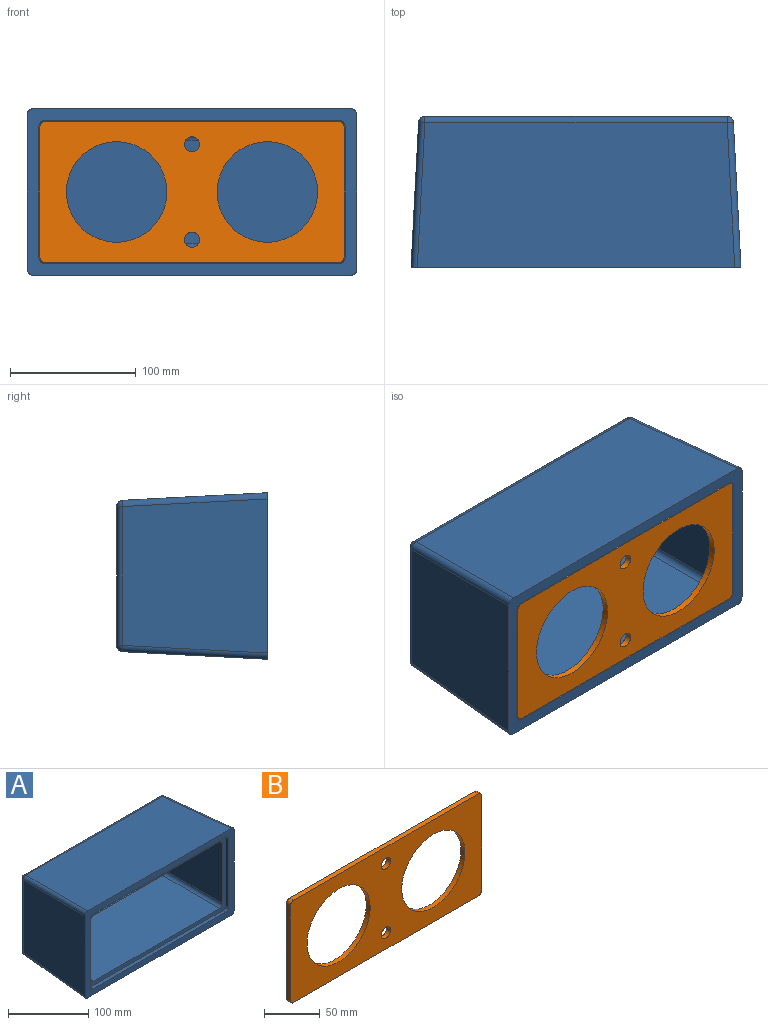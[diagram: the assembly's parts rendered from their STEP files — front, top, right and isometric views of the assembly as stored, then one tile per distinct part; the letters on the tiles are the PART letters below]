
ASSEMBLY  parts=2 mates=1
PART A: 44 faces, bbox 262.6x120.1x132.6 mm
  f0: plane 262.58x132.58mm, normal (0,-1,0), area 6996.1mm2, adj f1,f2,f3,f4,f6,f8,f11,f17
  f1: plane 252.59x115.26mm, normal (0,0.05,1), area 28456.9mm2, adj f0,f11,f15,f17
  f2: plane 122.59x115.26mm, normal (-1,0.05,0), area 13452.3mm2, adj f0,f8,f14,f17
  f3: plane 252.59x115.26mm, normal (0,0.05,-1), area 28456.9mm2, adj f0,f6,f8,f9
  f4: plane 122.59x115.26mm, normal (1,0.05,0), area 13452.3mm2, adj f0,f6,f10,f11
  f5: plane 240.51x110.51mm, normal (0,1,0), area 26578.9mm2, adj f9,f10,f14,f15
  f6: cylinder r=5mm len=115.48mm, axis (-0.05,1,0.05), area 906.7mm2, adj f0,f3,f4,f7
  f7: sphere r=5mm, area 36.7mm2, adj f6,f9,f10
  f8: cylinder r=5mm len=115.48mm, axis (0.05,1,0.05), area 906.7mm2, adj f0,f2,f3,f12
  f9: cylinder r=5mm len=240.51mm, axis (-1,0,0), area 1826mm2, adj f3,f5,f7,f12
  f10: cylinder r=5mm len=110.51mm, axis (0,0,1), area 839mm2, adj f4,f5,f7,f13
  f11: cylinder r=5mm len=115.48mm, axis (-0.05,1,-0.05), area 906.7mm2, adj f0,f1,f4,f13
  f12: sphere r=5mm, area 36.7mm2, adj f8,f9,f14
  f13: sphere r=5mm, area 36.7mm2, adj f10,f11,f15
  f14: cylinder r=5mm len=110.51mm, axis (0,0,1), area 839mm2, adj f2,f5,f12,f16
  f15: cylinder r=5mm len=240.51mm, axis (-1,0,0), area 1826mm2, adj f1,f5,f13,f16
  f16: sphere r=5mm, area 36.7mm2, adj f14,f15,f17
  f17: cylinder r=5mm len=115.48mm, axis (0.05,1,-0.05), area 906.7mm2, adj f0,f1,f2,f16
  f18: plane 244x114mm, normal (0,-1,0), area 4147.7mm2, adj f19,f20,f21,f22,f28,f29,f30,f31
  f19: plane 234x5mm, normal (0,0,-1), area 1170mm2, adj f0,f18,f40,f43
  f20: plane 104x5mm, normal (1,0,0), area 520mm2, adj f0,f18,f40,f41
  f21: plane 234x5mm, normal (0,0,1), area 1170mm2, adj f0,f18,f41,f42
  f22: plane 104x5mm, normal (-1,0,0), area 520mm2, adj f0,f18,f42,f43
  f23: plane 212.04x82.04mm, normal (0,-1,0), area 17396.2mm2, adj f24,f25,f26,f27
  f24: cylinder r=5mm len=212.04mm, axis (1,0,0), area 1609.9mm2, adj f23,f31,f35,f39
  f25: cylinder r=5mm len=82.04mm, axis (0,0,-1), area 622.9mm2, adj f23,f30,f37,f39
  f26: cylinder r=5mm len=212.04mm, axis (1,0,0), area 1609.9mm2, adj f23,f29,f33,f37
  f27: cylinder r=5mm len=82.04mm, axis (0,0,-1), area 622.9mm2, adj f23,f28,f33,f35
  f28: plane 95.26x92.03mm, normal (-1,-0.05,0), area 8302.4mm2, adj f18,f27,f32,f34
  f29: plane 222.03x95.26mm, normal (0,-0.05,1), area 20703.4mm2, adj f18,f26,f32,f36
  f30: plane 95.26x92.03mm, normal (1,-0.05,0), area 8302.4mm2, adj f18,f25,f36,f38
  f31: plane 222.03x95.26mm, normal (0,-0.05,-1), area 20703.4mm2, adj f18,f24,f34,f38
  f32: cylinder r=5mm len=95.48mm, axis (0.05,-1,-0.05), area 749.5mm2, adj f18,f28,f29,f33
  f33: sphere r=5mm, area 36.7mm2, adj f26,f27,f32
  f34: cylinder r=5mm len=95.48mm, axis (0.05,-1,0.05), area 749.5mm2, adj f18,f28,f31,f35
  f35: sphere r=5mm, area 36.7mm2, adj f24,f27,f34
  f36: cylinder r=5mm len=95.48mm, axis (-0.05,-1,-0.05), area 749.5mm2, adj f18,f29,f30,f37
  f37: sphere r=5mm, area 36.7mm2, adj f25,f26,f36
  f38: cylinder r=5mm len=95.48mm, axis (-0.05,-1,0.05), area 749.5mm2, adj f18,f30,f31,f39
  f39: sphere r=5mm, area 36.7mm2, adj f24,f25,f38
  f40: cylinder r=5mm len=5mm, axis (0,1,0), area 39.3mm2, adj f0,f18,f19,f20
  f41: cylinder r=5mm len=5mm, axis (0,-1,0), area 39.3mm2, adj f0,f18,f20,f21
  f42: cylinder r=5mm len=5mm, axis (0,1,0), area 39.3mm2, adj f0,f18,f21,f22
  f43: cylinder r=5mm len=5mm, axis (0,-1,0), area 39.3mm2, adj f0,f18,f19,f22
PART B: 14 faces, bbox 242x5x112 mm
  f0: plane 234x5mm, normal (0,0,1), area 1170mm2, adj f8,f9,f10,f13
  f1: plane 104x5mm, normal (-1,0,0), area 520mm2, adj f8,f9,f10,f11
  f2: plane 234x5mm, normal (0,0,-1), area 1170mm2, adj f8,f9,f11,f12
  f3: cylinder r=40mm len=80mm, axis (0,1,0), area 1256.6mm2, adj f8,f9
  f4: cylinder r=5.98mm len=11.97mm, axis (0,1,0), area 188mm2, adj f8,f9
  f5: cylinder r=5.98mm len=11.97mm, axis (0,1,0), area 188mm2, adj f8,f9
  f6: cylinder r=40mm len=80mm, axis (0,1,0), area 1256.6mm2, adj f8,f9
  f7: plane 104x5mm, normal (1,0,0), area 520mm2, adj f8,f9,f12,f13
  f8: plane 242x112mm, normal (0,-1,0), area 16812.2mm2, adj f0,f1,f2,f3,f4,f5,f6,f7
  f9: plane 242x112mm, normal (0,1,0), area 16812.2mm2, adj f0,f1,f2,f3,f4,f5,f6,f7
  f10: cylinder r=4mm len=5mm, axis (0,-1,0), area 31.4mm2, adj f0,f1,f8,f9
  f11: cylinder r=4mm len=5mm, axis (0,1,0), area 31.4mm2, adj f1,f2,f8,f9
  f12: cylinder r=4mm len=5mm, axis (0,-1,0), area 31.4mm2, adj f2,f7,f8,f9
  f13: cylinder r=4mm len=5mm, axis (0,1,0), area 31.4mm2, adj f0,f7,f8,f9
PLACE A t=(-166.16,-122.45,-43.53)mm
PLACE B t=(-166.16,-237.45,-43.53)mm
MATE slider B.f13 <-> A.f43  axis (0,1,0) through (-49.16,-237.45,8.47)mm
